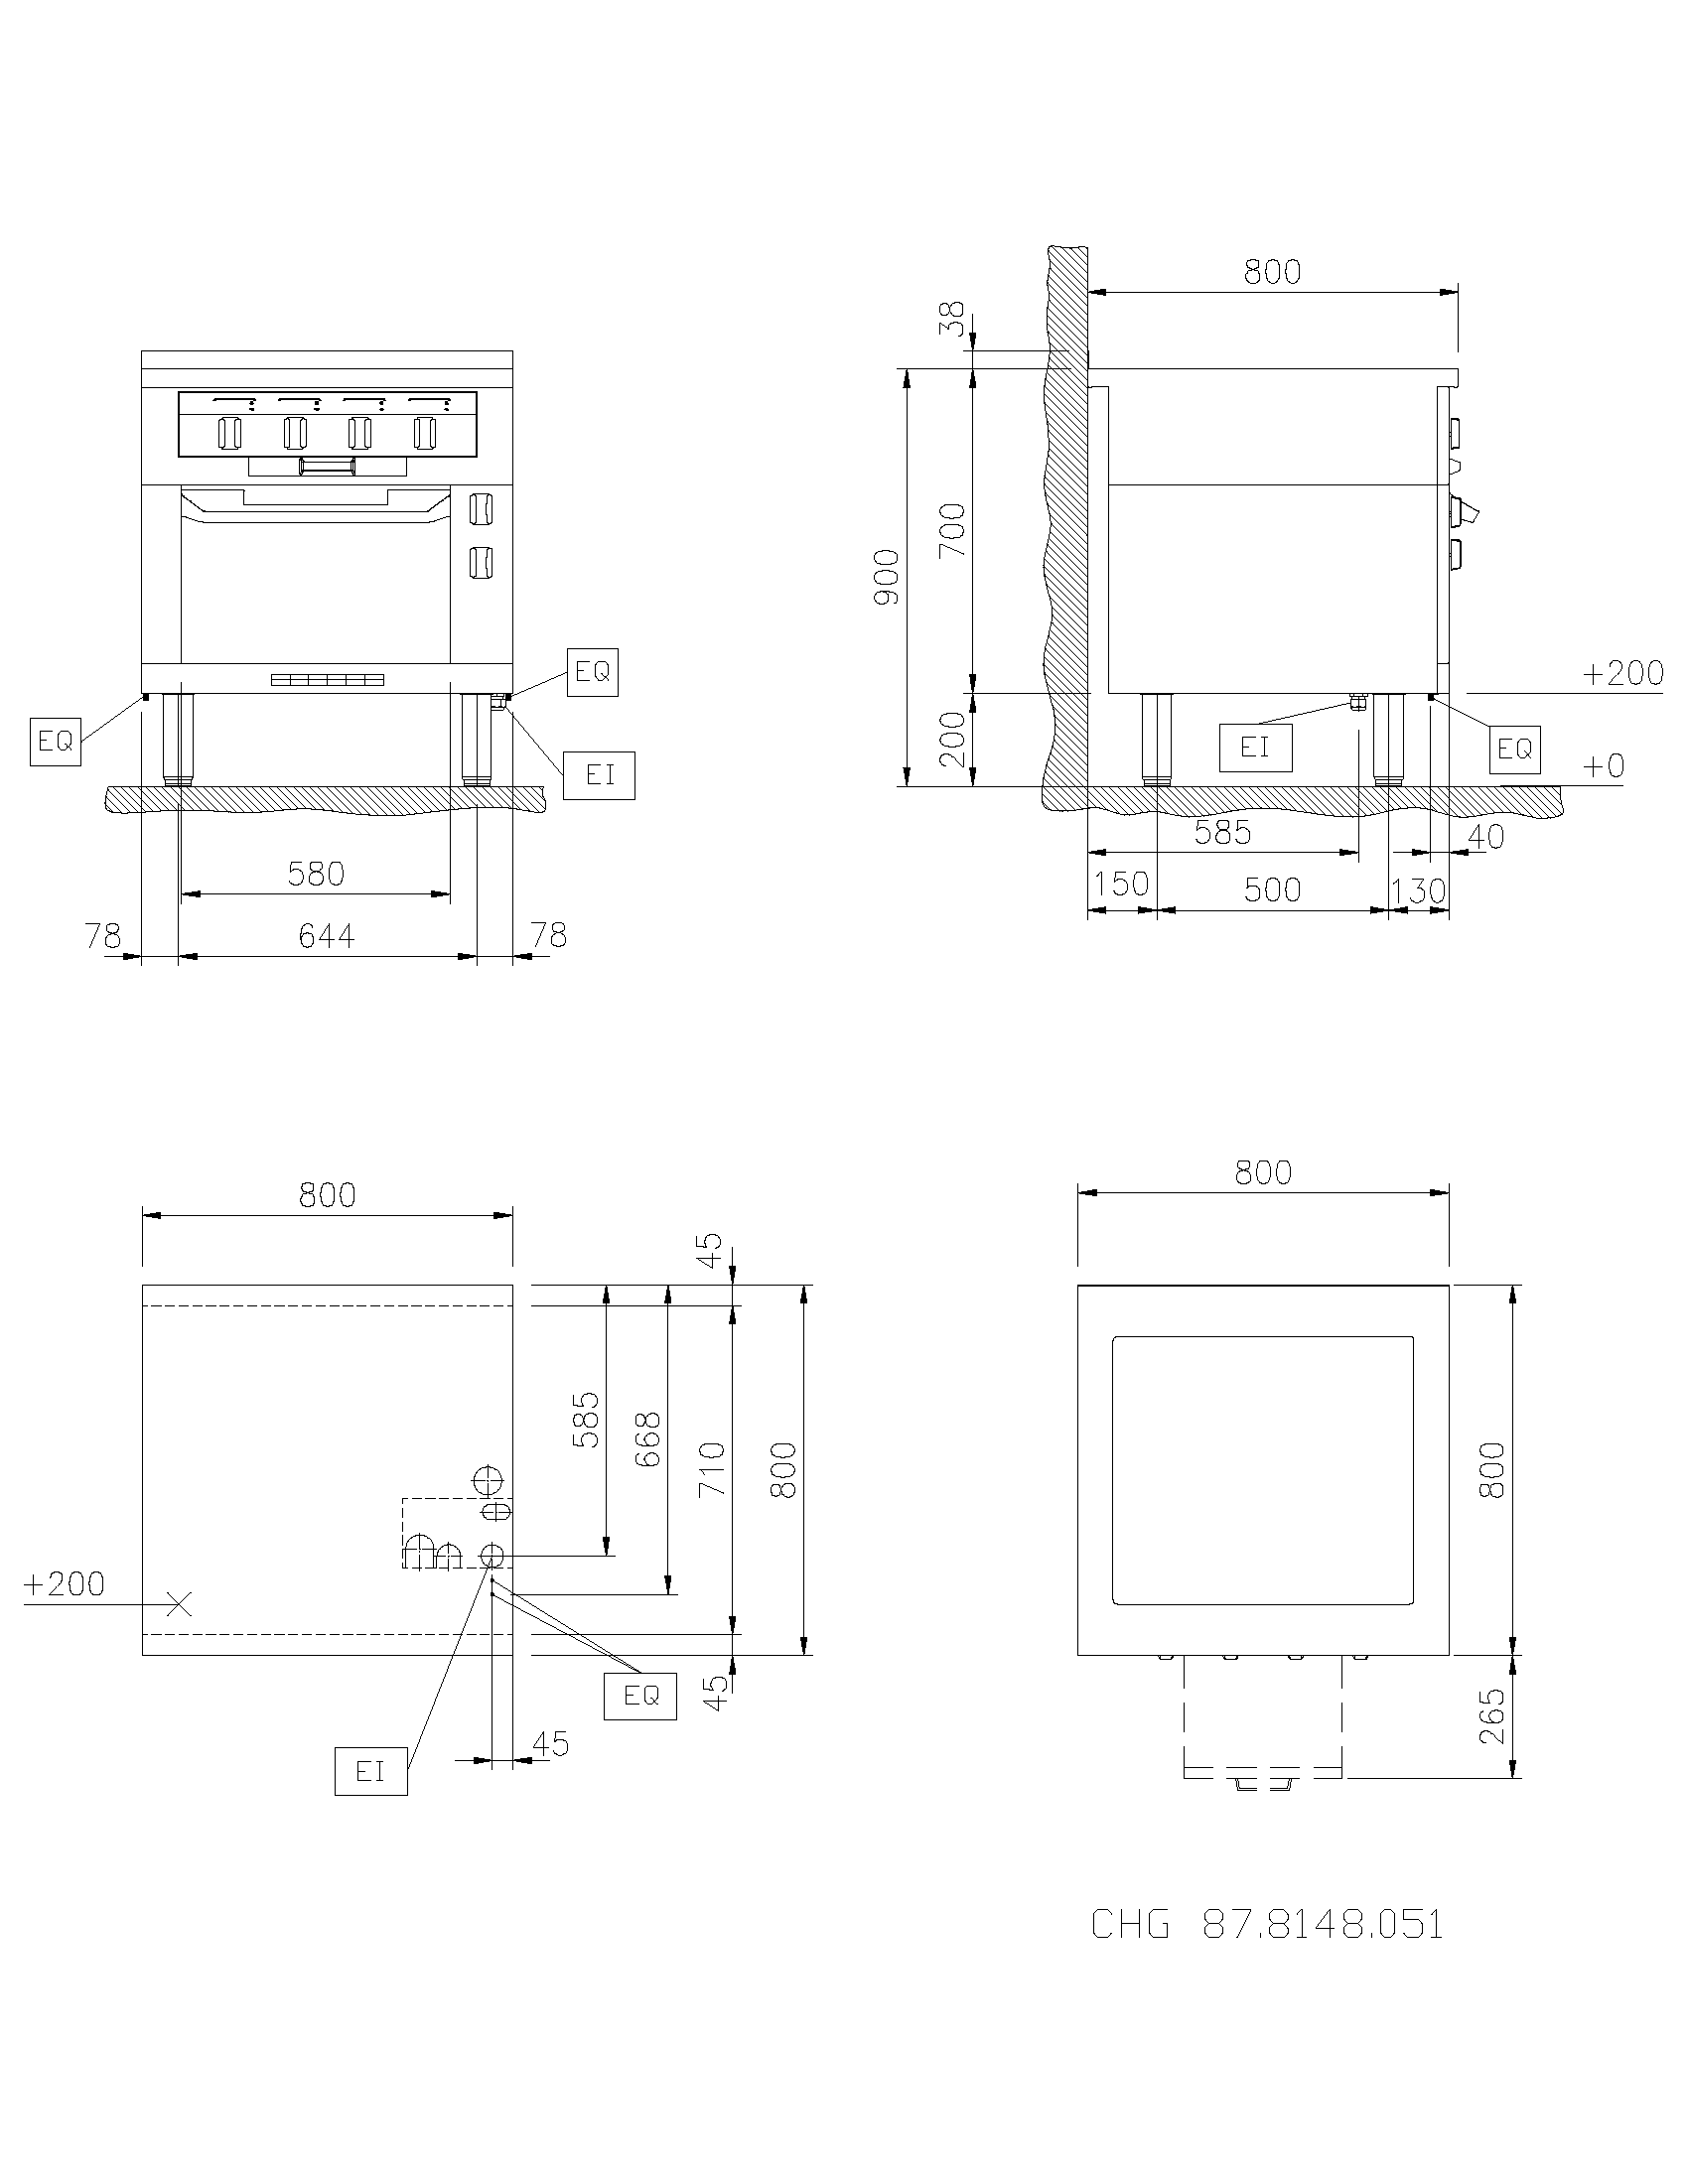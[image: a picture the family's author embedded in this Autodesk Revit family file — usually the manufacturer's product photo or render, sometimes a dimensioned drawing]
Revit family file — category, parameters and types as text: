
# Revit family: QF_ELECTROLUXPROFESSIONAL_589839_MCH1EAH1DM
name_source: partatom
category: Attrezzature speciali
units: mm (PartAtom-declared; Revit-internal decimal feet)

## family parameters
Basato su piano di lavoro = No
Condiviso = No
Punto di calcolo locali = No
Quota connettore circolare = Usa diametro
Sempre verticale = Sì
Taglio con vuoti quando caricato = No
Tipo di parte = Normale

## types (1)
- Standard
    Accessory = Sì
    Cold Water Size = 0"
    Compressed Air Pressure = 0.00 psi
    Compressed Air Size = 0"
    Compressed Air Volume = 0 GPM
    Condensate Return Size = 0"
    Cycle = 50 Hz
    Depth Actual = 900 mm  [stored 2.95276 ft]
    Descrizione = FRYTOP,H3,RBD,2Z,1S,800X900X700H MARINE
    Direct Waste Size = 0"
    Gas Input Pressure = 0.0
    Gas KW = 0
    Gas Size = 0"
    HP = 20.5 HP
    Height Actual = 700 mm  [stored 2.29659 ft]
    Hot Water Size = 0"
    Item Number = 589839
    Length Actual = 800 mm  [stored 2.62467 ft]
    Modello = MCH1EAH1DM
    Phase = 3
    Produttore = Electrolux Professional
    Prospetto di default = 0 mm  [stored 0 ft]
    Refrigerant Compressor Remote = Sì
    Refrigeration Liquid Line Size = 0 mm  [stored 0 ft]
    Refrigeration Suction Line Size = 0 mm  [stored 0 ft]
    Steam Consumption per Hour = 0
    Steam Supply Maximum Pressure = 0.00 psi
    Steam Supply Minimum Pressure = 0.00 psi
    Steam Supply Size = 0"
    URL = https://www.electroluxprofessional.com
    URL Manufacturer = https://www.electroluxprofessional.com
    Volts = 440 V
    Watts = 15300 W
    Weight = 150.00 kg

note: source unit labels omitted for Gas Input Pressure — the stored unit's dimension contradicts the parameter name (converter mislabeling)

note: [stored X ft] marks values corroborated as IEEE doubles in the binary element streams (Revit-internal decimal feet)

## geometry (parser evidence)
native form markers: Blend x13, Sweep x9
no freeform markers — native parametric forms only
